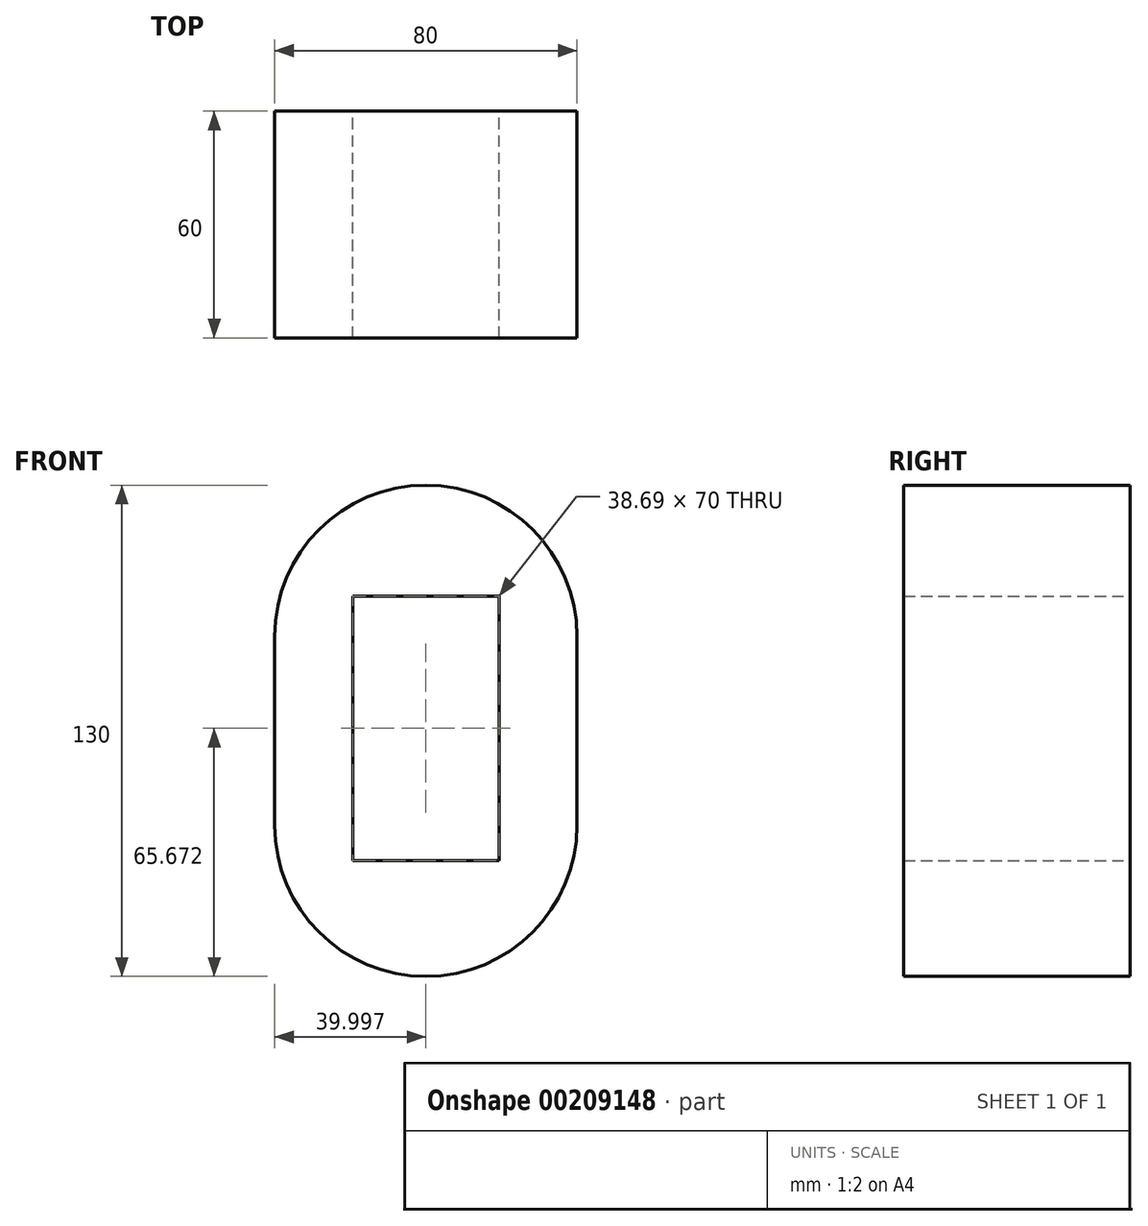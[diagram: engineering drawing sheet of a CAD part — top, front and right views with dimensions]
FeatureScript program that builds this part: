
annotation { "Feature Type Name" : "Feature", "Feature Type Description" : "" }
export const myFeature = defineFeature(function(context is Context, id is Id, definition is map)
    precondition{}
    {
        {
            var Q0;
            Q0=qCreatedBy(makeId("Front.planeOp"),FACE);
            var sketch = newSketch(context, id + "F0", { "sketchPlane" : qUnion([Q0])});
            skLineSegment(sketch, "E0", {"start": v(-22.43, 40.5) * mm, "end": v(16.26, 40.5) * mm});
            skLineSegment(sketch, "E1", {"start": v(-22.43, 40.5) * mm, "end": v(-22.43, -29.5) * mm});
            skLineSegment(sketch, "E2", {"start": v(-22.43, -29.5) * mm, "end": v(16.26, -29.5) * mm});
            skLineSegment(sketch, "E3", {"start": v(16.26, -29.5) * mm, "end": v(16.26, 40.5) * mm});
            skArc(sketch, "E4", {"start": v(-43.08, 29.82) * mm, "mid": v(-31.37, 58.1) * mm, "end": v(-3.08, 69.82) * mm});
            skArc(sketch, "E5", {"start": v(36.92, 29.82) * mm, "mid": v(25.2, 58.1) * mm, "end": v(-3.08, 69.82) * mm});
            skLineSegment(sketch, "E6", {"start": v(-43.08, 29.82) * mm, "end": v(-43.08, -20.18) * mm});
            skLineSegment(sketch, "E7", {"start": v(36.92, -20.18) * mm, "end": v(36.92, 29.82) * mm});
            skArc(sketch, "E8", {"start": v(-43.08, -20.18) * mm, "mid": v(-3.08, -60.18) * mm, "end": v(36.92, -20.18) * mm});
            skSolve(sketch);
        }
        {
            var Q0;
            Q0=makeQuery(id+"F0.imprint","IMPRINT",FACE,{"disambiguationData":[TD([[makeQuery(id+"F0.imprint","IMPRINT",EDGE,{"derivedFrom":sQuery(id+"F0.wireOp",EDGE,"E0")}),1.0]])]});
            extrude(context, id + "F1", {"entities" : qUnion([Q0]), "depth" : 60 * mm});
        }
    });
